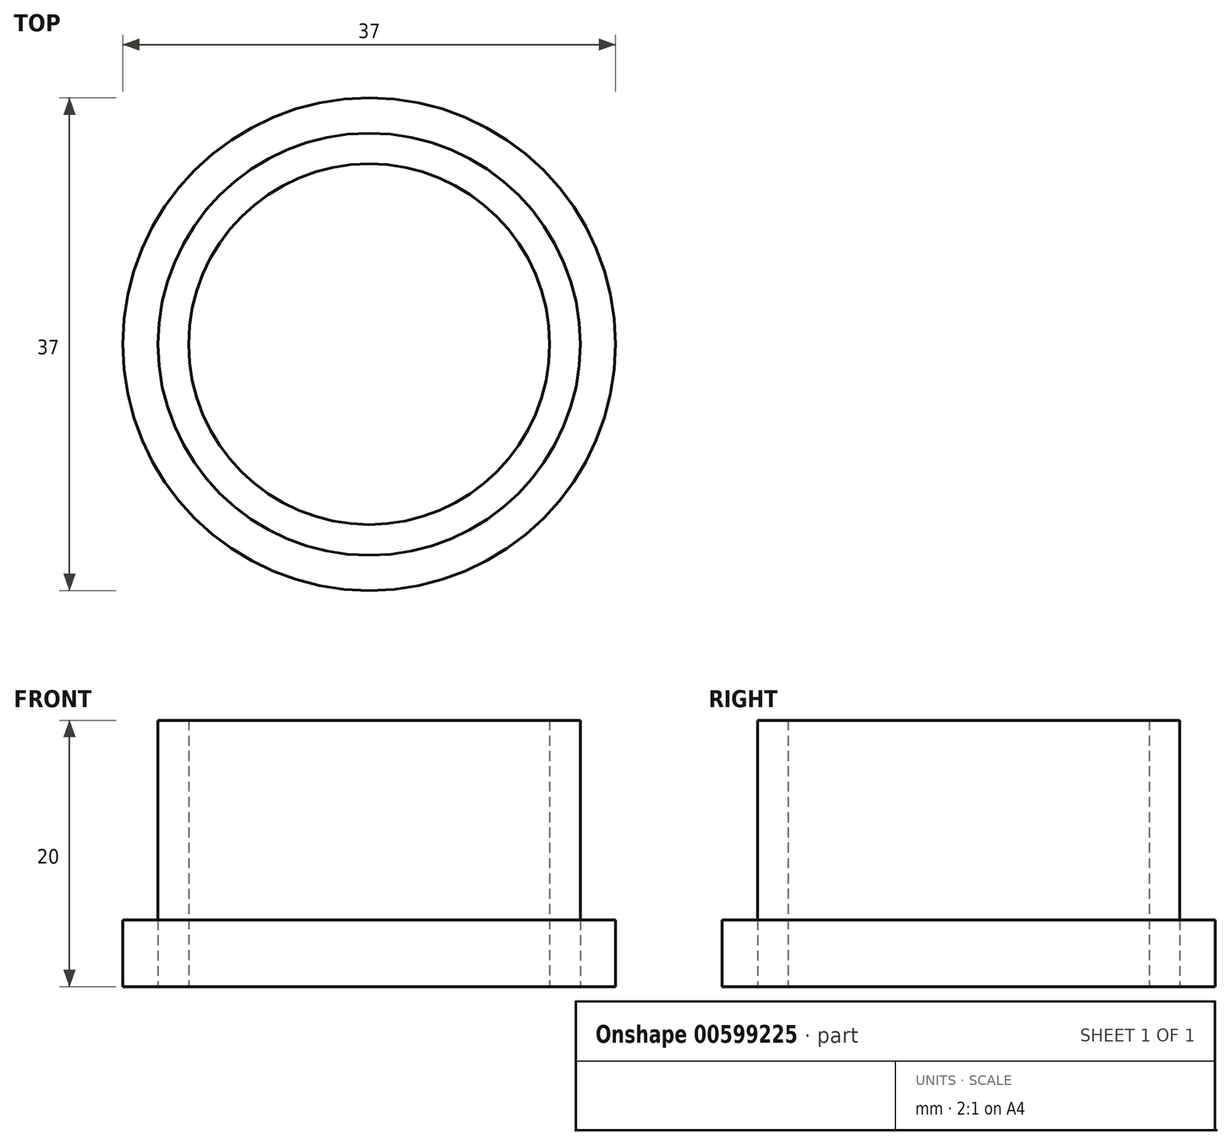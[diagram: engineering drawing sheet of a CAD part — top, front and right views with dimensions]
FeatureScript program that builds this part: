
annotation { "Feature Type Name" : "Feature", "Feature Type Description" : "" }
export const myFeature = defineFeature(function(context is Context, id is Id, definition is map)
    precondition{}
    {
        {
            var Q0;
            Q0=qCreatedBy(makeId("Top.planeOp"),FACE);
            var sketch = newSketch(context, id + "F0", { "sketchPlane" : qUnion([Q0])});
            skCircle(sketch, "E0", {"center": v(0, 0) * mm, "radius": 18.5 * mm});
            skCircle(sketch, "E1", {"center": v(0, 0) * mm, "radius": 15.85 * mm});
            skCircle(sketch, "E2", {"center": v(0, 0) * mm, "radius": 13.55 * mm});
            skSolve(sketch);
        }
        {
            var Q0;
            Q0=makeQuery(id+"F0.imprint","IMPRINT",FACE,{"disambiguationData":[TD([[makeQuery(id+"F0.imprint","IMPRINT",EDGE,{"derivedFrom":sQuery(id+"F0.wireOp",EDGE,"E1")}),1.0]])]});
            extrude(context, id + "F1", {"entities" : qUnion([Q0]), "depth" : 20 * mm, "offsetDistance" : 25 * mm});
        }
        {
            var Q0;
            Q0=makeQuery(id+"F0.imprint","IMPRINT",FACE,{"disambiguationData":[TD([[makeQuery(id+"F0.imprint","IMPRINT",EDGE,{"derivedFrom":sQuery(id+"F0.wireOp",EDGE,"E0")}),1.0]])]});
            extrude(context, id + "F2", {"entities" : qUnion([Q0]), "depth" : 5 * mm, "offsetDistance" : 25 * mm});
        }
    });
